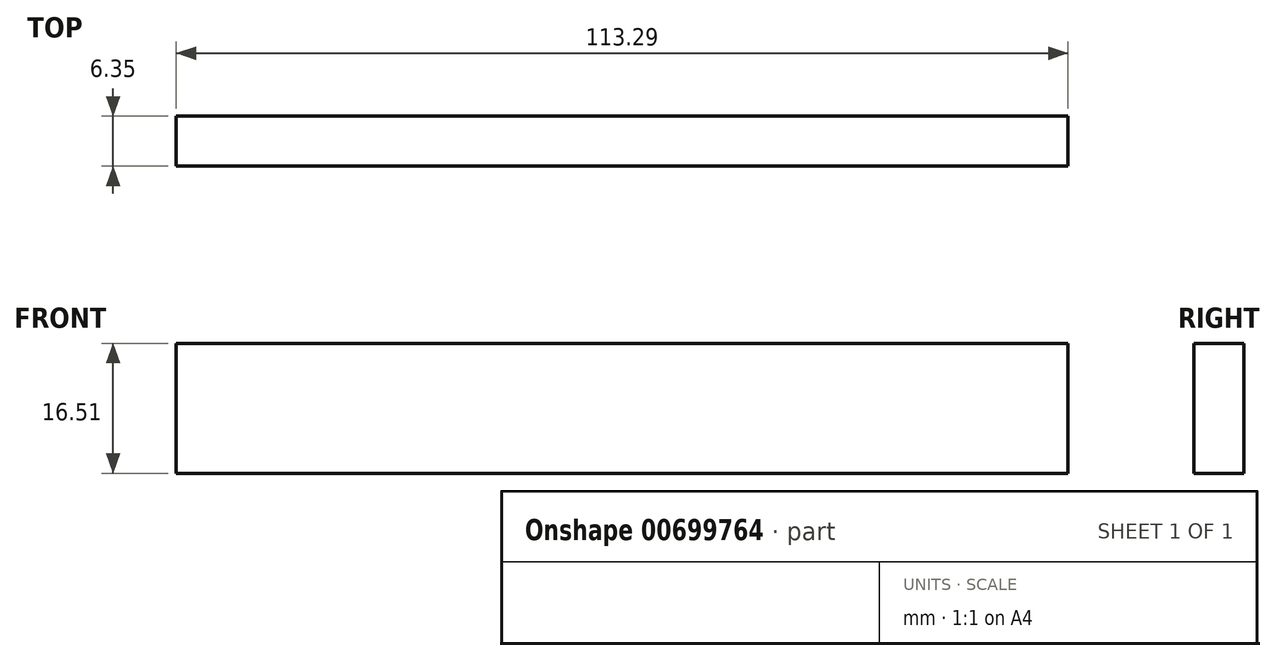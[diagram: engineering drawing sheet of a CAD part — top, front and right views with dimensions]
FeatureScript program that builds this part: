
annotation { "Feature Type Name" : "Feature", "Feature Type Description" : "" }
export const myFeature = defineFeature(function(context is Context, id is Id, definition is map)
    precondition{}
    {
        {
            var Q0;
            Q0=qCreatedBy(makeId("Front.planeOp"),FACE);
            var sketch = newSketch(context, id + "F0", { "sketchPlane" : qUnion([Q0])});
            skLineSegment(sketch, "E0.bottom", {"start": v(-74.63, 32.16) * mm, "end": v(38.66, 32.16) * mm});
            skLineSegment(sketch, "E0.top", {"start": v(-74.63, 15.65) * mm, "end": v(38.66, 15.65) * mm});
            skLineSegment(sketch, "E0.left", {"start": v(-74.63, 32.16) * mm, "end": v(-74.63, 15.65) * mm});
            skLineSegment(sketch, "E0.right", {"start": v(38.66, 32.16) * mm, "end": v(38.66, 15.65) * mm});
            skSolve(sketch);
        }
        {
            var Q0;
            Q0=makeQuery(id+"F0.imprint","IMPRINT",FACE,{"disambiguationData":[TD([[makeQuery(id+"F0.imprint","IMPRINT",EDGE,{"derivedFrom":sQuery(id+"F0.wireOp",EDGE,"E0.bottom")}),-1.0]])]});
            extrude(context, id + "F1", {"entities" : qUnion([Q0]), "depth" : 6.35 * mm, "offsetDistance" : 25.4 * mm});
        }
    });
